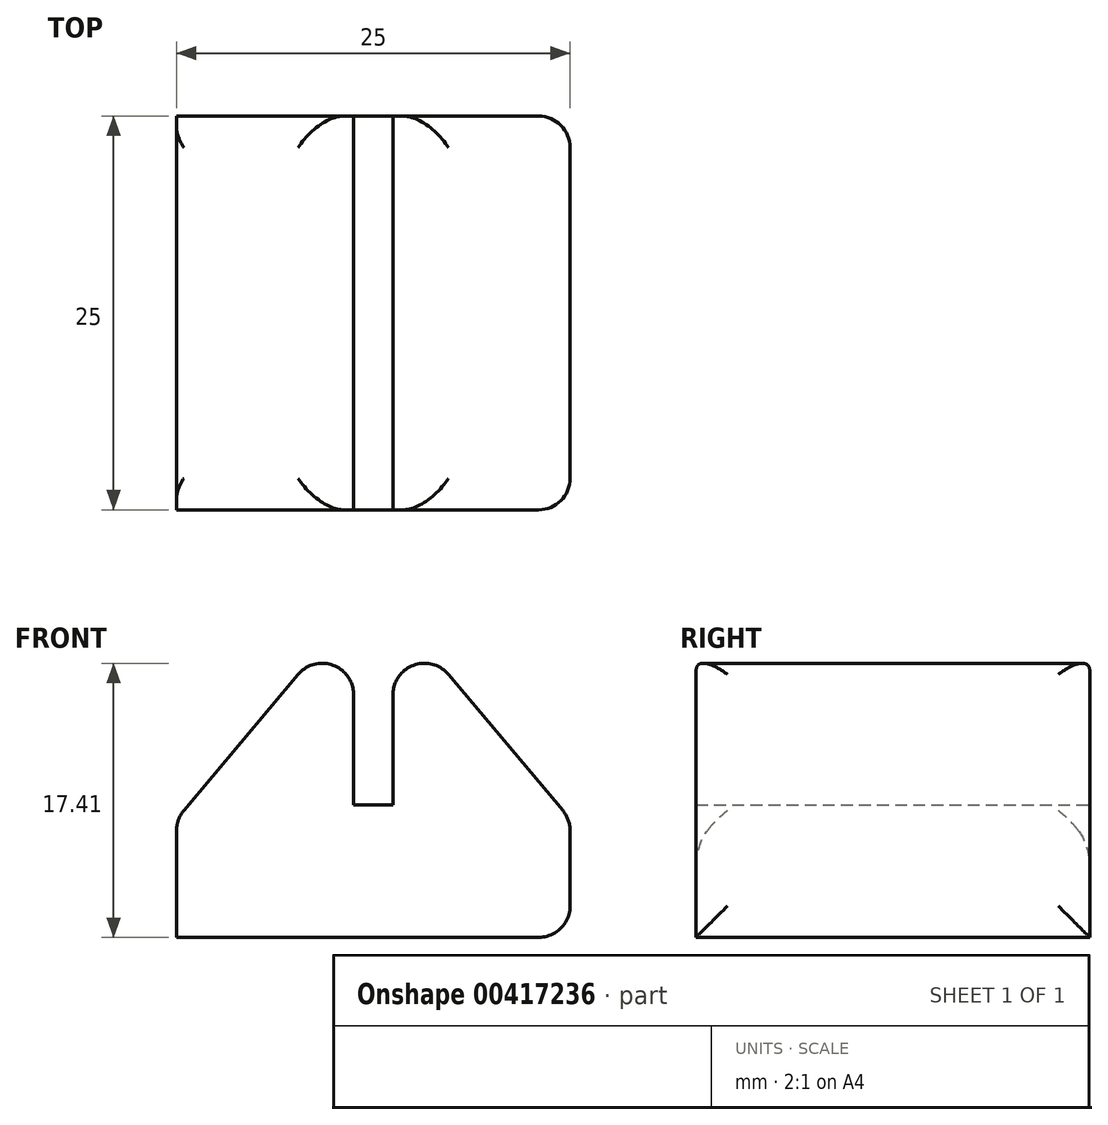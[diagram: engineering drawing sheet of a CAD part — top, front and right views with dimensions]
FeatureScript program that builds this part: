
annotation { "Feature Type Name" : "Feature", "Feature Type Description" : "" }
export const myFeature = defineFeature(function(context is Context, id is Id, definition is map)
    precondition{}
    {
        {
            var Q0;
            Q0=qCreatedBy(makeId("Front.planeOp"),FACE);
            var sketch = newSketch(context, id + "F0", { "sketchPlane" : qUnion([Q0])});
            skLineSegment(sketch, "E0", {"start": v(-12.5, 0) * mm, "end": v(12.5, 0) * mm});
            skLineSegment(sketch, "E1.bottom", {"start": v(-12.5, 0) * mm, "end": v(-12.5, 0) * mm});
            skLineSegment(sketch, "E1.top", {"start": v(-12.5, 7.5) * mm, "end": v(-12.5, 7.5) * mm});
            skLineSegment(sketch, "E1.left", {"start": v(-12.5, 0) * mm, "end": v(-12.5, 7.5) * mm});
            skLineSegment(sketch, "E1.right", {"start": v(-12.5, 0) * mm, "end": v(-12.5, 7.5) * mm});
            skLineSegment(sketch, "E2", {"start": v(12.5, 0) * mm, "end": v(12.5, 7.5) * mm});
            skLineSegment(sketch, "E3", {"start": v(-12.5, 7.5) * mm, "end": v(-1.25, 20.9) * mm});
            skLineSegment(sketch, "E4", {"start": v(12.5, 7.5) * mm, "end": v(1.25, 20.9) * mm});
            skLineSegment(sketch, "E5", {"start": v(-1.25, 20.9) * mm, "end": v(-1.25, 8.4) * mm});
            skLineSegment(sketch, "E6", {"start": v(1.25, 20.9) * mm, "end": v(1.25, 8.4) * mm});
            skLineSegment(sketch, "E7", {"start": v(-1.25, 8.4) * mm, "end": v(1.25, 8.4) * mm});
            skSolve(sketch);
        }
        {
            var Q0;
            Q0=makeQuery(id+"F0.imprint","IMPRINT",FACE,{"disambiguationData":[TD([[makeQuery(id+"F0.imprint","IMPRINT",EDGE,{"derivedFrom":sQuery(id+"F0.wireOp",EDGE,"E0")}),1.0]])]});
            extrude(context, id + "F1", {"entities" : qUnion([Q0]), "depth" : 25 * mm});
        }
        {
            var Q0;
            Q0=makeQuery(id+"F1.opExtrude","SWEPT_FACE",FACE,{"disambiguationData":[OSD([sQuery(id+"F0.wireOp",EDGE,"E4")])]});
            var Q1;
            Q1=makeQuery(id+"F1.opExtrude","SWEPT_FACE",FACE,{"disambiguationData":[OSD([sQuery(id+"F0.wireOp",EDGE,"E2")])]});
            fillet(context, id + "F2", {"entities" : qUnion([Q0, Q1]), "radius" : 2 * mm, "tangentPropagation" : true, "allowEdgeOverflow" : false});
        }
        {
            var Q0;
            Q0=makeQuery(id+"F1.opExtrude","SWEPT_FACE",FACE,{"disambiguationData":[OSD([sQuery(id+"F0.wireOp",EDGE,"E1.right")])]});
            var Q1;
            Q1=makeQuery(id+"F1.opExtrude","SWEPT_FACE",FACE,{"disambiguationData":[OSD([sQuery(id+"F0.wireOp",EDGE,"E3")])]});
            fillet(context, id + "F3", {"entities" : qUnion([Q0, Q1]), "radius" : 2 * mm, "tangentPropagation" : true, "allowEdgeOverflow" : false});
        }
    });
